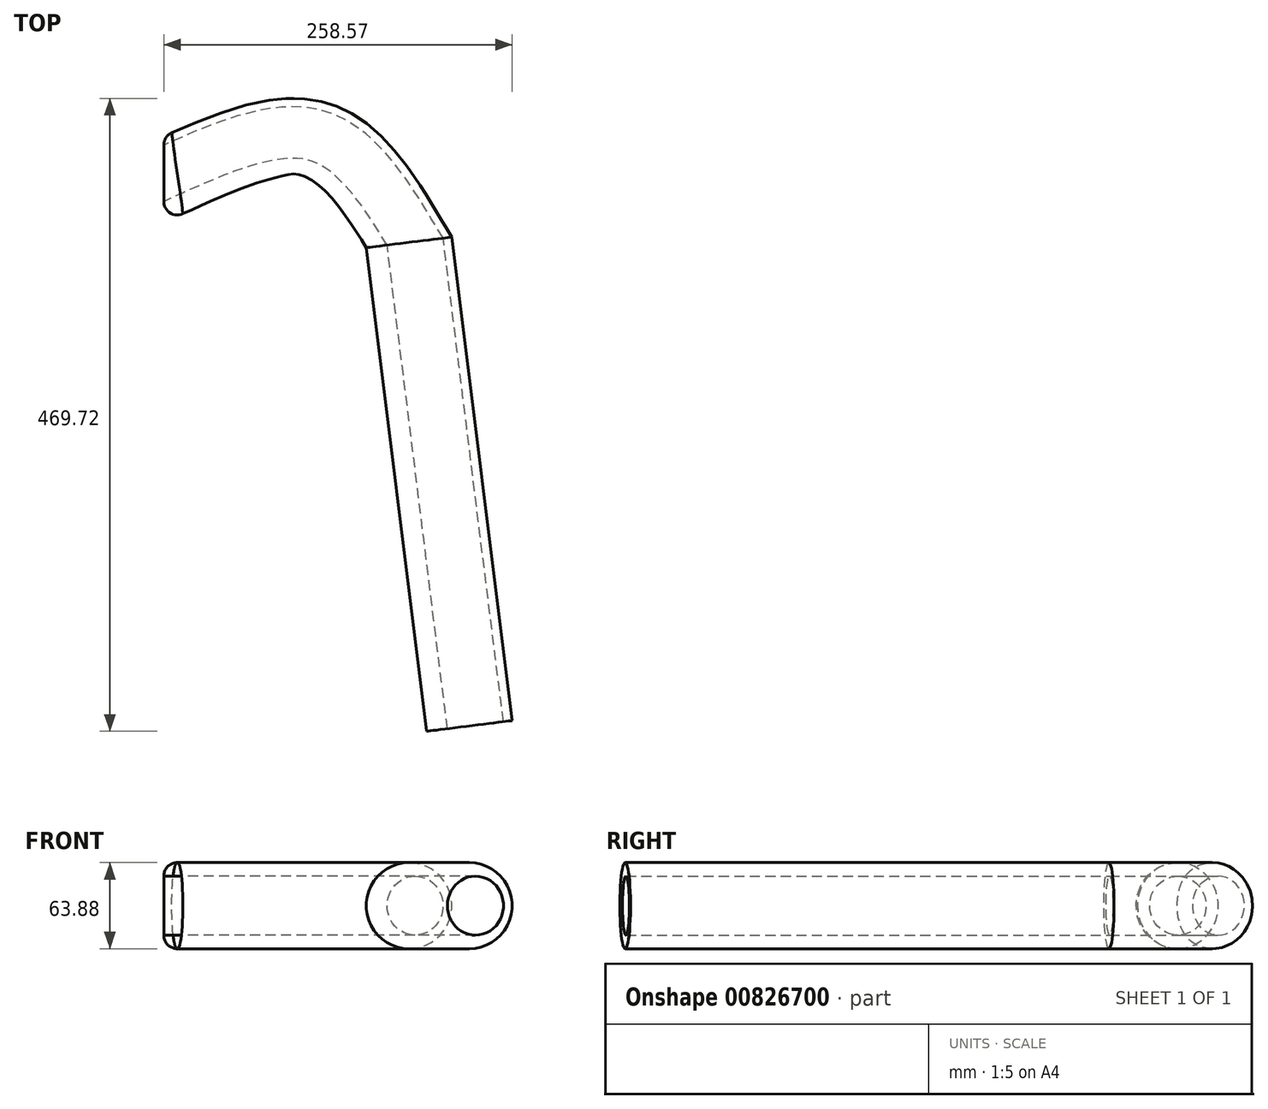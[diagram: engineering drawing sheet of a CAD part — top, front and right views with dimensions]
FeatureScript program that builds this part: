
annotation { "Feature Type Name" : "Feature", "Feature Type Description" : "" }
export const myFeature = defineFeature(function(context is Context, id is Id, definition is map)
    precondition{}
    {
        {
            var Q0;
            Q0=qCreatedBy(makeId("Right.planeOp"),FACE);
            var sketch = newSketch(context, id + "F0", { "sketchPlane" : qUnion([Q0])});
            skCircle(sketch, "E0", {"center": v(0, 0) * mm, "radius": 31.94 * mm});
            skSolve(sketch);
        }
        {
            var Q0;
            Q0=qCreatedBy(makeId("Top.planeOp"),FACE);
            var sketch = newSketch(context, id + "F1", { "sketchPlane" : qUnion([Q0])});
            skFitSpline(sketch, "E1", {"points": [v(0, 0) * mm, v(113, 27.74) * mm, v(182.06, -46.73) * mm], "startDerivative": vector(238.11, 107.4) * mm, "endDerivative": vector(124.72, -204.39) * mm});
            skSolve(sketch);
        }
        {
            var Q0;
            Q0=makeQuery(id+"F0.imprint","IMPRINT",FACE,{"disambiguationData":[TD([[makeQuery(id+"F0.imprint","IMPRINT",EDGE,{"derivedFrom":sQuery(id+"F0.wireOp",EDGE,"E0")}),1.0]])]});
            var Q1;
            Q1=sQuery(id+"F1.wireOp",EDGE,"E1");
            sweep(context, id + "F2", {"profiles" : qUnion([Q0]), "path" : qUnion([Q1])});
        }
        {
            var Q0;
            Q0=makeQuery(id+"F2.opSweep","CAP_EDGE",EDGE,{"disambiguationData":[OSD([sQuery(id+"F0.wireOp",EDGE,"E0"),sQuery(id+"F1.wireOp",VERTEX,"E1.start")])],"isStart":true});
            fillet(context, id + "F3", {"entities" : qUnion([Q0]), "radius" : 10 * mm, "tangentPropagation" : true, "allowEdgeOverflow" : false});
        }
        {
            var Q0;
            Q0=makeQuery(id+"F2.opSweep","CAP_FACE",FACE,{"disambiguationData":[OSD([sQuery(id+"F0.wireOp",EDGE,"E0"),sQuery(id+"F1.wireOp",VERTEX,"E1.start")])],"isStart":true});
            var Q1;
            Q1=sQuery(id+"F1.wireOp",EDGE,"E1");
            sweep(context, id + "F4", {"operationType" : NewBodyOperationType.REMOVE, "profiles" : qUnion([Q0]), "path" : qUnion([Q1])});
        }
        {
            var Q0;
            Q0=makeQuery(id+"F2.opSweep","CAP_FACE",FACE,{"disambiguationData":[OSD([sQuery(id+"F0.wireOp",EDGE,"E0"),sQuery(id+"F1.wireOp",VERTEX,"E1.end")])],"isStart":false});
            extrude(context, id + "F5", {"entities" : qUnion([Q0]), "operationType" : NewBodyOperationType.ADD, "depth" : 361.77 * mm, "offsetDistance" : 25 * mm});
        }
    });
